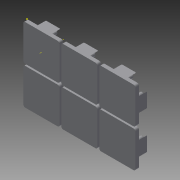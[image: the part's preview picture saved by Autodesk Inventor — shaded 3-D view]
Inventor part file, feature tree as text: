
AUTODESK INVENTOR PART (.ipt)
format: ipt  version: 2015 (Build 190159000, 159)  size: 495,616 bytes
history: native  units: mm
features: fillet x3, sketch x3, extrude x2, other x1, pattern_circular x1, pattern_linear x1
ambient origin geometry x8: Origin, YZ Plane, XZ Plane, XY Plane, X Axis, Y Axis, Z Axis, Center Point
bodies: Solid1 (feature_tree)
feature tree (11):
  extrude  "Extrusion1"  Depth=20.0mm
  extrude  "Extrusion2"  Depth=4.0mm
  fillet  "Fillet1"  Radius=5.5mm
  fillet  "Fillet2"  Radius=1.8mm
  fillet  "Fillet3"  [1 undecoded]
  sketch  "Sketch3"  dims[d8=4.5mm d9=0.0mm d10=1.0mm d11=1.0mm d12=0.4mm d13=40.0mm d14=360.0deg d16=20.0mm d18=21.0mm d19=30.0mm d21=21.0mm]
  other  "Work Axis1"
  pattern_circular  "Circular Pattern1"  [2 undecoded]
  pattern_linear  "Rectangular Pattern1"  Spacing1=1.0mm  [1 undecoded]
  sketch  "Sketch1"  dims[d0=20.0mm d1=20.0mm]
  sketch  "Sketch2"  dims[d2=2.0mm d3=0.0mm d4=4.0mm d5=5.5mm d6=1.8mm d7=45.0deg]
note: 4 required parameter values undecoded (feature->parameter linkage not recoverable at this tier; creation-order binding heuristic only, values carry confidence <= 0.55)
